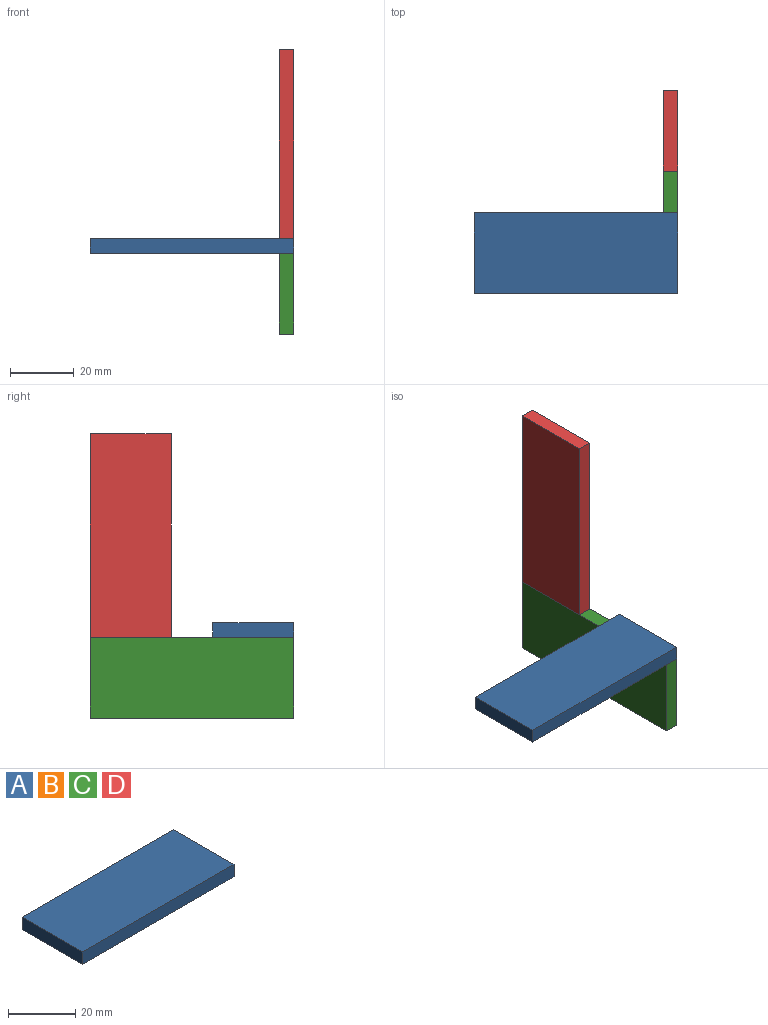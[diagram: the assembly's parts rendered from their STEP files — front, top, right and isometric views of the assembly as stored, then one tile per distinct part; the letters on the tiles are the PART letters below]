
ASSEMBLY  parts=4 mates=1
PART A: 6 faces, bbox 63.8x25.4x4.5 mm
  f0: plane 63.78x25.4mm, normal (0,0,1), area 1620mm2, adj f1,f3,f4,f5
  f1: plane 25.4x4.52mm, normal (-1,0,0), area 114.9mm2, adj f0,f2,f4,f5
  f2: plane 63.78x25.4mm, normal (0,0,-1), area 1620mm2, adj f1,f3,f4,f5
  f3: plane 25.4x4.52mm, normal (1,0,0), area 114.9mm2, adj f0,f2,f4,f5
  f4: plane 63.78x4.52mm, normal (0,-1,0), area 288.5mm2, adj f0,f1,f2,f3
  f5: plane 63.78x4.52mm, normal (0,1,0), area 288.5mm2, adj f0,f1,f2,f3
PART B: same geometry as A
PART C: same geometry as A
PART D: same geometry as A
PLACE A at identity
PLACE B at identity fixed
PLACE C rot(axis=(-0.58,-0.58,0.58),120deg) t=(59.48,6.49,2.19)mm
PLACE D rot(axis=(0.71,0,-0.71),180deg) t=(59.48,12.98,59.48)mm
MATE fastened B.f2 <-> C.f4  axis (0,0,1) through (31.89,-25.4,27.59)mm
